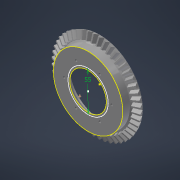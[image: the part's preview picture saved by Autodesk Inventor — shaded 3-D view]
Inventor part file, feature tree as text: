
AUTODESK INVENTOR PART (.ipt)
format: ipt  version: 2022 (Build 260153000, 153)  size: 898,048 bytes
history: native  units: mm
features: other x26, sketch x7, extrude x3, chamfer x3, projected_geometry x3, reference x3, loft x2, pattern_circular x2, hole x1
ambient origin geometry x6: Origin, XZ Plane, X Axis, Y Axis, Z Axis, Center Point
bodies: Solid1 (feature_tree)
feature tree (50):
  other  "Top Point"
  other  "Mesh Plane2"
  other  "Teeth Body"
  other  "Start Point"
  other  "Tooth Plane"
  other  "Start Sketch"
  other  "End Point"
  other  "3D Sketch Right"
  other  "End Plane Right"
  loft  "Loft Right"
  pattern_circular  "Circular Pattern Right"  [2 undecoded]
  other  "3D Sketch Left"
  other  "End Plane Left"
  loft  "Loft Left"
  pattern_circular  "Circular Pattern Left"  [2 undecoded]
  other  "Fix Body"
  sketch  "Sketch15"  dims[d2=121.840242mm]
  extrude  "Extrusion6"  Depth=10.0mm
  chamfer  "Chamfer3"  Distance=120.781755mm
  sketch  "Sketch17"  dims[d4=21.425483mm]
  extrude  "Extrusion7"  TaperAngle=0.0deg  [1 undecoded]
  extrude  "Extrusion8"  Depth=10.0mm TaperAngle=0.0deg
  chamfer  "Chamfer4"  Angle=360.0deg  [1 undecoded]
  chamfer  "Chamfer6"  Distance=428.686656mm
  hole  "Hole3"  [1 undecoded]
  sketch  "Sketch21"  dims[d8=55.203225mm d9=143.656013mm d11=10.275mm d12=47.611121mm d15=46.413249mm d16=120.781755mm d17=0.0mm d18=90.0deg d19=0.0mm d20=90.0deg d21=480.0mm d22=360.0deg d26=428.686656mm d27=3.781698mm d28=120.0mm d29=-11.938871mm d30=47.611121mm d31=46.413249mm d32=120.781755mm d35=0.0mm d37=0.0mm d39=0.0mm d40=90.0deg d41=480.0mm d42=360.0deg d46=90.0deg d47=90.0deg d48=0.0mm d49=0.0mm d50=90.0deg d51=0.654498mm d52=0.0mm d53=0.0mm d54=0.0mm d56=18.960921mm d57=167.172015mm d58=159.362015mm d59=140.553318mm d60=133.9869mm d61=140.553318mm d62=133.9869mm d65=428.686656mm d66=31.5mm d67=120.0mm d68=-11.938871mm d69=3.781698mm d70=46.413249mm d71=120.781755mm d72=47.611121mm d73=133.9869mm d74=140.553318mm d75=0.0mm d77=0.0mm d79=0.0mm d80=90.0deg d81=480.0mm d82=360.0deg d84=10.0mm d85=20.0mm d86=20.0mm d87=10.0mm d88=0.0mm d89=0.0mm d90=90.0deg d91=90.0deg d92=90.0deg d93=90.0deg d137=50.0mm d138=95.0mm d139=12.0mm d140=0.0mm d141=2.0mm d142=2.0mm d143=45.0deg d144=0.0mm d145=0.0mm d146=10.0mm d147=0.0mm d148=5.0mm d149=2.0mm d150=45.0deg d156=5.0mm d157=2.0mm d158=45.0deg d159=65.0mm d160=60.0mm d162=360.0deg d164=3.242mm d165=6.0mm d166=8.0mm d167=4.6mm d168=90.0deg d169=8.0mm d170=20.594885mm d171=55.0mm d95=0.5mm d96=0.872665mm d97=0.5mm d98=0.872665mm]
  other  "Mesh Plane"
  other  "Top Plane"
  other  "Teeth Body Sketch"
  other  "End Plane"
  other  "End Sketch"
  other  "Helical Curve Left"
  other  "End Sketch Left"
  other  "Body Sketch"
  sketch  "Sketch6"  dims[d0=120.0mm d1=117.791709mm]
  other  "Srf1"
  other  "Helical Curve Right"
  other  "End Sketch Right"
  projected_geometry  "Projected Loop5"
  sketch  "Sketch16"  dims[d3=10.0mm]
  projected_geometry  "Projected Loop6"
  sketch  "Sketch18"  dims[d5=90.0deg]
  reference  "Reference4"
  reference  "Reference5"
  reference  "Reference6"
  sketch  "Sketch20"  dims[d7=56.627956mm]
  projected_geometry  "Projected Loop7"
  other  "Pitch Diameter"
  other  "SistemaDeElevación.iam"
  other  "Tuerca2:1"
note: 7 required parameter values undecoded (feature->parameter linkage not recoverable at this tier; creation-order binding heuristic only, values carry confidence <= 0.55)
